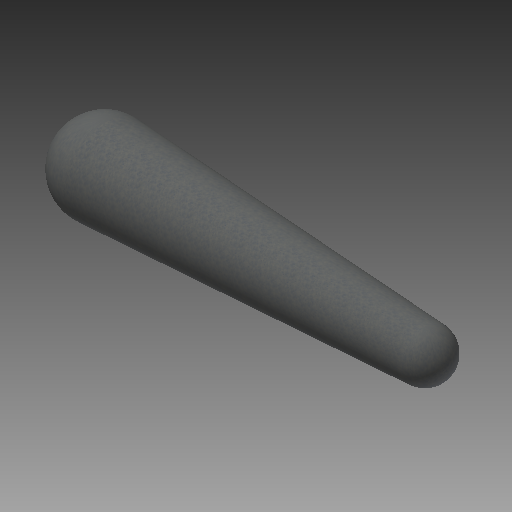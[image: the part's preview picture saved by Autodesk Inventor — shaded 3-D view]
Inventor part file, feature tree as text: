
AUTODESK INVENTOR PART (.ipt)
format: ipt  version: 2022 (Build 260153000, 153)  size: 203,776 bytes
history: native  units: mm (DEFAULTED — no unit token found)
features: other x1, revolve x1, sketch x1
ambient origin geometry x8: Origin, YZ Plane, XZ Plane, XY Plane, X Axis, Y Axis, Z Axis, Center Point
bodies: Solid1 (feature_tree)
feature tree (3):
  other  "iMandy - 2D BODY"
  revolve  "Revolution1"  [1 undecoded]
  sketch  "Sketch1"  dims[d1=10.0mm d16=234.95mm d17=115.824mm d18=67.818mm d19=90.0deg d20=473.202mm]
note: 1 required parameter value undecoded (feature->parameter linkage not recoverable at this tier; creation-order binding heuristic only, values carry confidence <= 0.55)
